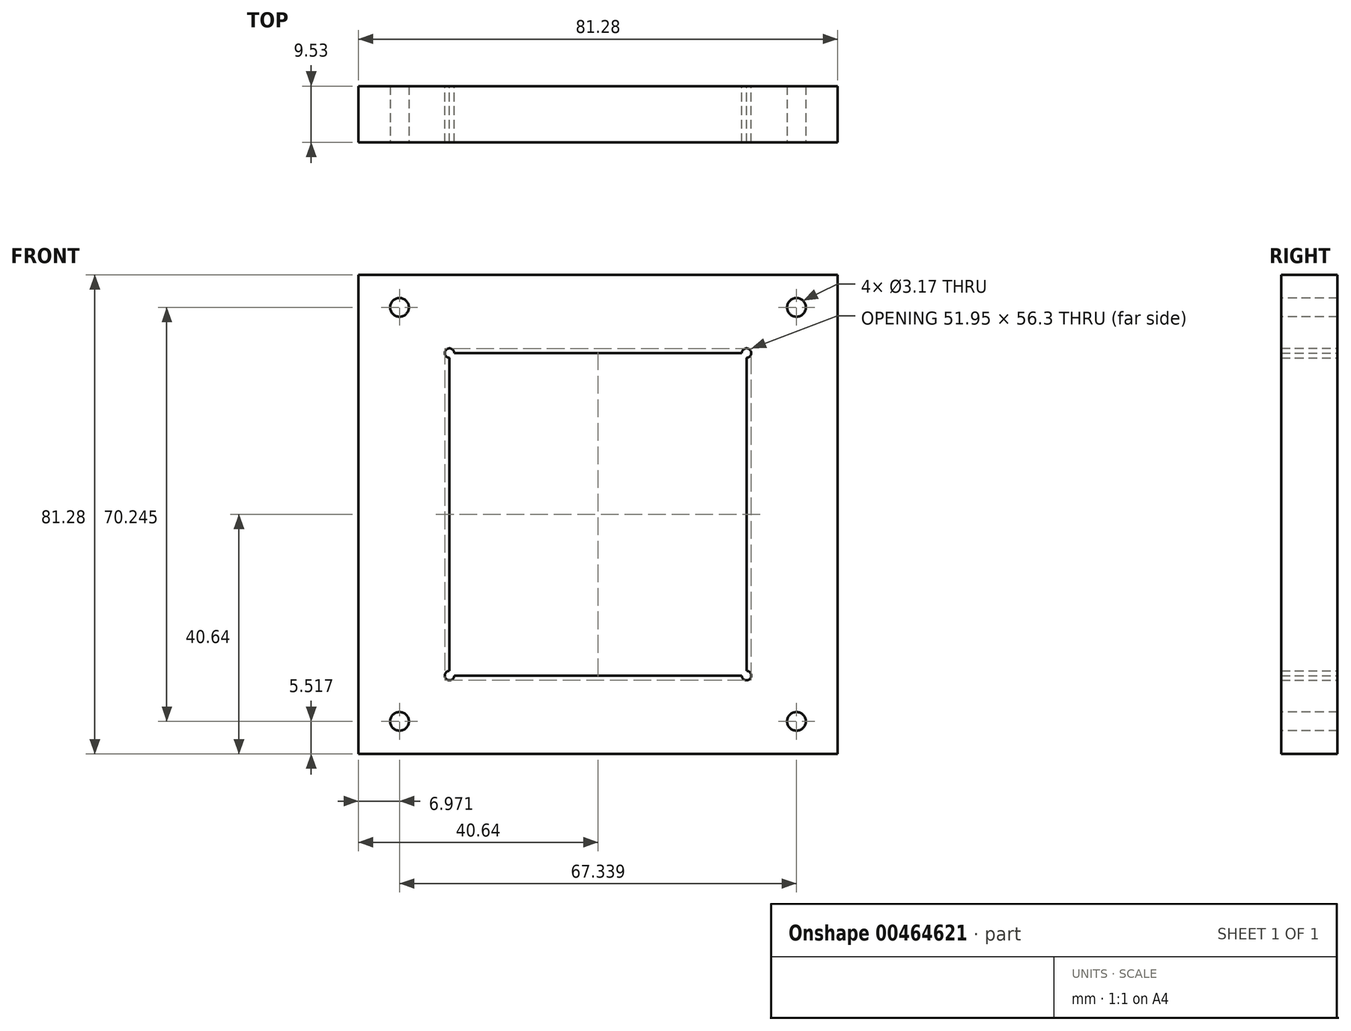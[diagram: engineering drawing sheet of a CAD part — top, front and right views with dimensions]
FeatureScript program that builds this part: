
annotation { "Feature Type Name" : "Feature", "Feature Type Description" : "" }
export const myFeature = defineFeature(function(context is Context, id is Id, definition is map)
    precondition{}
    {
        {
            var Q0;
            Q0=qCreatedBy(makeId("Front.planeOp"),FACE);
            var sketch = newSketch(context, id + "F0", { "sketchPlane" : qUnion([Q0])});
            skLineSegment(sketch, "E0.bottom", {"start": v(-40.64, 40.64) * mm, "end": v(40.64, 40.64) * mm});
            skLineSegment(sketch, "E0.top", {"start": v(-40.64, -40.64) * mm, "end": v(40.64, -40.64) * mm});
            skLineSegment(sketch, "E0.left", {"start": v(-40.64, 40.64) * mm, "end": v(-40.64, -40.64) * mm});
            skLineSegment(sketch, "E0.right", {"start": v(40.64, 40.64) * mm, "end": v(40.64, -40.64) * mm});
            skLineSegment(sketch, "E1.bottom", {"start": v(-25.19, 27.36) * mm, "end": v(25.19, 27.36) * mm});
            skLineSegment(sketch, "E1.top", {"start": v(-25.19, -27.36) * mm, "end": v(25.19, -27.36) * mm});
            skLineSegment(sketch, "E1.left", {"start": v(-25.19, 27.36) * mm, "end": v(-25.19, -27.36) * mm});
            skLineSegment(sketch, "E1.right", {"start": v(25.19, 27.36) * mm, "end": v(25.19, -27.36) * mm});
            skLineSegment(sketch, "E2", {"start": v(25.19, 27.36) * mm, "end": v(-25.19, -27.36) * mm, "construction": true});
            skLineSegment(sketch, "E3", {"start": v(40.64, 40.64) * mm, "end": v(-40.64, -40.64) * mm, "construction": true});
            skSolve(sketch);
        }
        {
            var Q0;
            Q0 = qSketchRegion(id + "F0", true);
            var Q1;
            Q1 = qSketchRegion(id + "FM1T2SSERqG8d5W_0", true);
            var Q2;
            Q2=sQuery(id+"F0.wireOp",EDGE,"E1.bottom");
            var Q3;
            Q3=sQuery(id+"F0.wireOp",EDGE,"E1.left");
            var Q4;
            Q4=sQuery(id+"F0.wireOp",EDGE,"E1.right");
            var Q5;
            Q5=sQuery(id+"F0.wireOp",EDGE,"E1.top");
            var Q6;
            Q6=sQuery(id+"F0.wireOp",EDGE,"E0.bottom");
            extrude(context, id + "F1", {"entities" : qUnion([Q0, Q1]), "surfaceEntities" : qUnion([Q2, Q3, Q4, Q5, Q6]), "offsetDistance" : 25.4 * mm, "depth" : 9.52 * mm});
        }
        {
            var Q0;
            Q0=makeQuery(id+"F1.opExtrude","CAP_FACE",FACE,{"disambiguationData":[OSD([sQuery(id+"F0.wireOp",EDGE,"E0.bottom"),sQuery(id+"F0.wireOp",EDGE,"E0.top"),sQuery(id+"F0.wireOp",EDGE,"E0.left"),sQuery(id+"F0.wireOp",EDGE,"E0.right"),sQuery(id+"F0.wireOp",EDGE,"E1.bottom"),sQuery(id+"F0.wireOp",EDGE,"E1.top"),sQuery(id+"F0.wireOp",EDGE,"E1.left"),sQuery(id+"F0.wireOp",EDGE,"E1.right")])],"isStart":false});
            var sketch = newSketch(context, id + "F2", { "sketchPlane" : qUnion([Q0])});
            skPoint(sketch, "E4", {"position": v(-33.67, 35.12) * mm});
            skLineSegment(sketch, "E5", {"start": v(0, 40.64) * mm, "end": v(0, -40.64) * mm, "construction": true});
            skLineSegment(sketch, "E6", {"start": v(-40.64, 0) * mm, "end": v(40.64, 0) * mm, "construction": true});
            skPoint(sketch, "E7.MirrorP", {"position": v(33.67, 35.12) * mm});
            skPoint(sketch, "E8.MirrorP", {"position": v(-33.67, -35.12) * mm});
            skPoint(sketch, "E9.MirrorP", {"position": v(33.67, -35.12) * mm});
            skSolve(sketch);
        }
        {
            var Q0;
            Q0=sQuery(id+"F2.wireOp",VERTEX,"E4");
            var Q1;
            Q1=sQuery(id+"F2.wireOp",VERTEX,"E7.MirrorP");
            var Q2;
            Q2=sQuery(id+"F2.wireOp",VERTEX,"E8.MirrorP");
            var Q3;
            Q3=sQuery(id+"F2.wireOp",VERTEX,"E9.MirrorP");
            var Q4;
            Q4=makeQuery(id+"F1.opExtrude","SWEPT_BODY",BODY,{"disambiguationData":[OSD([sQuery(id+"F0.wireOp",EDGE,"E0.bottom"),sQuery(id+"F0.wireOp",EDGE,"E0.top"),sQuery(id+"F0.wireOp",EDGE,"E0.left"),sQuery(id+"F0.wireOp",EDGE,"E0.right"),sQuery(id+"F0.wireOp",EDGE,"E1.bottom"),sQuery(id+"F0.wireOp",EDGE,"E1.top"),sQuery(id+"F0.wireOp",EDGE,"E1.left"),sQuery(id+"F0.wireOp",EDGE,"E1.right")])]});
            hole(context, id + "F3", {"style" : HoleStyle.SIMPLE, "endStyle" : HoleEndStyle.THROUGH, "holeDiameter" : 3.17 * mm, "majorDiameter" : 6.35 * mm, "isTappedThrough" : true, "tappedDepth" : 12.7 * mm, "tapClearance" : 3, "locations" : qUnion([Q0, Q1, Q2, Q3]), "scope" : qUnion([Q4])});
        }
        {
            var Q0;
            Q0=sQuery(id+"F0.wireOp",VERTEX,"E1.bottom.end");
            var Q1;
            Q1=sQuery(id+"F0.wireOp",VERTEX,"E1.left.start");
            var Q2;
            Q2=sQuery(id+"F0.wireOp",VERTEX,"E1.top.start");
            var Q3;
            Q3=sQuery(id+"F0.wireOp",VERTEX,"E1.top.end");
            var Q4;
            Q4=makeQuery(id+"F1.opExtrude","SWEPT_BODY",BODY,{"disambiguationData":[OSD([sQuery(id+"F0.wireOp",EDGE,"E0.bottom"),sQuery(id+"F0.wireOp",EDGE,"E0.top"),sQuery(id+"F0.wireOp",EDGE,"E0.left"),sQuery(id+"F0.wireOp",EDGE,"E0.right"),sQuery(id+"F0.wireOp",EDGE,"E1.bottom"),sQuery(id+"F0.wireOp",EDGE,"E1.top"),sQuery(id+"F0.wireOp",EDGE,"E1.left"),sQuery(id+"F0.wireOp",EDGE,"E1.right")])]});
            hole(context, id + "F4", {"style" : HoleStyle.SIMPLE, "endStyle" : HoleEndStyle.THROUGH, "oppositeDirection" : true, "holeDiameter" : 1.6 * mm, "majorDiameter" : 6.35 * mm, "isTappedThrough" : true, "tappedDepth" : 12.7 * mm, "tapClearance" : 3, "locations" : qUnion([Q0, Q1, Q2, Q3]), "scope" : qUnion([Q4])});
        }
    });
